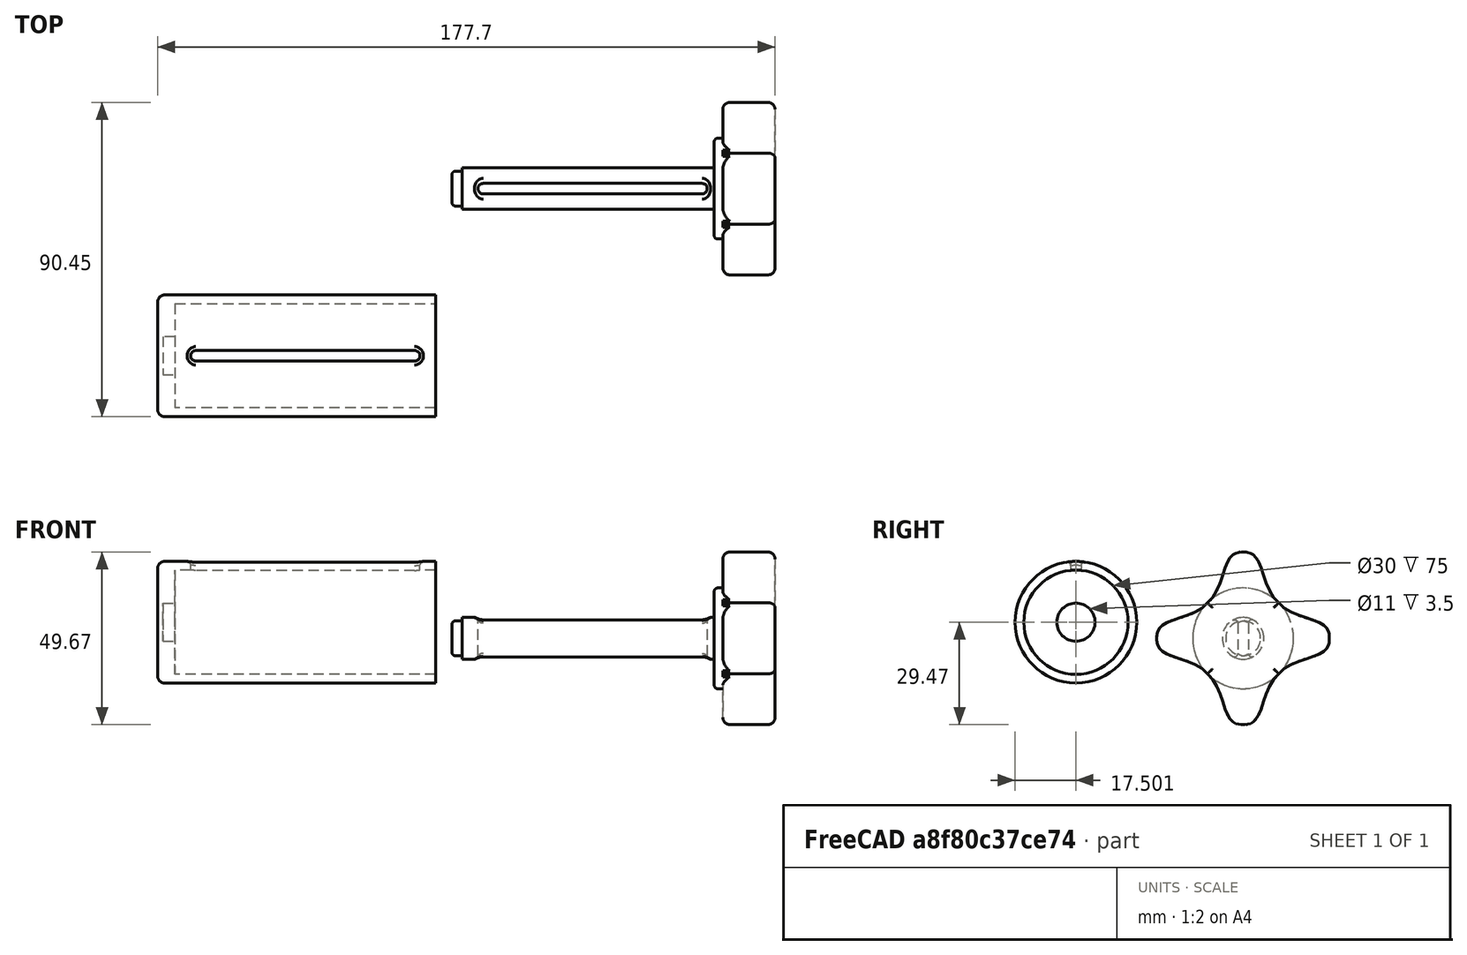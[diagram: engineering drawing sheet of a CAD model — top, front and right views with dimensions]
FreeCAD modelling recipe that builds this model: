
FCSTD DOCUMENT  (FreeCAD 1.0R39285 (Git))
Label: tomato_paste_squeezer
License: All rights reserved
objects: Sketcher::SketchObject×10, PartDesign::Pad×6, PartDesign::Pocket×4, PartDesign::Fillet×4, PartDesign::Body×2, App::Link×2, App::FeaturePython×2, PartDesign::Plane×1, PartDesign::PolarPattern×1, Assembly::JointGroup×1, Assembly::AssemblyObject×1
note: 67 computed .brp shape members not serialized (recipe doc carries the construction recipe); baked Part::Feature solids carry a one-line shape summary decoded from their .brp

FEATURE [Sketcher::SketchObject] Sketch
  ArcFitTolerance = 1e-06
  AttachmentSupport = -> [YZ_Plane]
  FullyConstrained = true
  MakeInternals = false
  MapMode = 5
  Placement = pos=(0,0,0) rot=(0.57735,0.57735,0.57735;2.0944rad)
  sketch-geometry (2):
    g0: Circle CenterX=0 CenterY=0 CenterZ=0 NormalX=0 NormalY=0 NormalZ=1 AngleXU=0 Radius=15
    g1: Circle CenterX=0 CenterY=0 CenterZ=0 NormalX=0 NormalY=0 NormalZ=1 AngleXU=0 Radius=17.5
  constraints (4):
    c: Diameter(g0) = 30
    c: Coincident(g0,g-1)
    c: Diameter(g1) = 35
    c: Coincident(g1,g0)
FEATURE [PartDesign::Pad] Pad
  Direction = (1,0,0)
  Length = 75
  Length2 = 10
  Placement = pos=(0,0,0) rot=(1,1,1;2.0944rad)
  Profile = -> Sketch
  ReferenceAxis = -> Sketch [N_Axis]
  Refine = true
  Suppressed = false
  Type = 0
FEATURE [PartDesign::Plane] DatumPlane
  AttachmentOffset = pos=(0,0,17.5) rot=(0,0,1;0rad)
  AttachmentSupport = -> [XY_Plane]
  Length = 114.142
  MapMode = 5
  Placement = pos=(0,0,17.5) rot=(0,0,1;0rad)
  ResizeMode = 0
  Width = 64.1421
FEATURE [Sketcher::SketchObject] Sketch001
  ArcFitTolerance = 1e-06
  AttachmentSupport = -> [DatumPlane]
  ExternalGeometry = -> [Pad]
  FullyConstrained = true
  MakeInternals = false
  MapMode = 5
  Placement = pos=(0,0,17.5) rot=(0,0,1;0rad)
  sketch-geometry (4):
    g0: ArcOfCircle CenterX=6 CenterY=0 CenterZ=0 NormalX=0 NormalY=0 NormalZ=1 AngleXU=0 Radius=1.5 StartAngle=1.5708 EndAngle=4.71239
    g1: ArcOfCircle CenterX=69 CenterY=0 CenterZ=0 NormalX=0 NormalY=0 NormalZ=1 AngleXU=0 Radius=1.5 StartAngle=4.71239 EndAngle=7.85398
    g2: LineSegment StartX=6 StartY=1.5 StartZ=0 EndX=69 EndY=1.5 EndZ=0
    g3: LineSegment StartX=6 StartY=-1.5 StartZ=0 EndX=69 EndY=-1.5 EndZ=0
  constraints (10):
    c: Tangent(g0,g2) = 1.5708
    c: Tangent(g0,g3) = -1.5708
    c: Tangent(g1,g2) = 1.5708
    c: Tangent(g1,g3) = -1.5708
    c: Equal(g0,g1)
    c: Horizontal(g3)
    c: Radius(g0) = 1.5
    c: PointOnObject(g0,g-1)
    c: DistanceX(g2,g2) = 63
    c: Distance(g0,g-1) = 6
FEATURE [PartDesign::Pocket] Pocket
  BaseFeature = -> Pad
  Direction = (0,0,-1)
  Length = 5
  Length2 = 5
  Placement = pos=(0,0,0) rot=(1,1,1;2.0944rad)
  Profile = -> Sketch001
  ReferenceAxis = -> Sketch001 [N_Axis]
  Refine = true
  Suppressed = false
  Type = 2
FEATURE [Sketcher::SketchObject] Sketch002
  ArcFitTolerance = 1e-06
  AttachmentSupport = -> [Pocket]
  FullyConstrained = true
  MakeInternals = false
  MapMode = 5
  Placement = pos=(0,0,0) rot=(0.57735,0.57735,-0.57735;4.18879rad)
  sketch-geometry (1):
    g0: Circle CenterX=0 CenterY=0 CenterZ=0 NormalX=0 NormalY=0 NormalZ=1 AngleXU=0 Radius=17.5
  constraints (2):
    c: Diameter(g0) = 35
    c: Coincident(g0,g-1)
FEATURE [PartDesign::Pad] Pad001
  BaseFeature = -> Pocket
  Direction = (-1,0,0)
  Length = 5
  Length2 = 10
  Placement = pos=(0,0,0) rot=(1,1,1;2.0944rad)
  Profile = -> Sketch002
  ReferenceAxis = -> Sketch002 [N_Axis]
  Refine = true
  Suppressed = false
  Type = 0
FEATURE [Sketcher::SketchObject] Sketch003
  ArcFitTolerance = 1e-06
  AttachmentSupport = -> [YZ_Plane001]
  FullyConstrained = true
  MakeInternals = false
  MapMode = 5
  Placement = pos=(0,0,0) rot=(0.57735,0.57735,0.57735;2.0944rad)
  sketch-geometry (1):
    g0: Circle CenterX=0 CenterY=0 CenterZ=0 NormalX=0 NormalY=0 NormalZ=1 AngleXU=0 Radius=14.5
  constraints (2):
    c: Diameter(g0) = 29
    c: Coincident(g0,g-1)
FEATURE [PartDesign::Pad] Pad002
  Direction = (1,0,0)
  Length = 2.5
  Length2 = 10
  Placement = pos=(0,0,0) rot=(1,1,1;2.0944rad)
  Profile = -> Sketch003
  ReferenceAxis = -> Sketch003 [N_Axis]
  Refine = true
  Suppressed = false
  Type = 0
FEATURE [Sketcher::SketchObject] Sketch004
  ArcFitTolerance = 1e-06
  AttachmentSupport = -> [Pad002]
  FullyConstrained = true
  MakeInternals = false
  MapMode = 5
  Placement = pos=(2.5,-6e-16,3e-16) rot=(0.57735,0.57735,0.57735;2.0944rad)
  sketch-geometry (1):
    g0: Circle CenterX=0 CenterY=0 CenterZ=0 NormalX=0 NormalY=0 NormalZ=1 AngleXU=0 Radius=25
  constraints (2):
    c: Diameter(g0) = 50
    c: Coincident(g0,g-1)
FEATURE [PartDesign::Pad] Pad003
  BaseFeature = -> Pad002
  Direction = (1,0,0)
  Length = 15
  Length2 = 10
  Placement = pos=(0,0,0) rot=(1,1,1;2.0944rad)
  Profile = -> Sketch004
  ReferenceAxis = -> Sketch004 [N_Axis]
  Refine = true
  Suppressed = false
  Type = 0
FEATURE [Sketcher::SketchObject] Sketch005
  ArcFitTolerance = 1e-06
  AttachmentSupport = -> [Pad003]
  ExternalGeometry = -> [Pad003]
  FullyConstrained = true
  MakeInternals = false
  MapMode = 5
  Placement = pos=(17.5,-3.9e-15,1.9e-15) rot=(0.57735,0.57735,0.57735;2.0944rad)
  sketch-geometry (20):
    g0: LineSegment [constr] StartX=0 StartY=0 StartZ=0 EndX=-10.253 EndY=10.253 EndZ=0
    g1: LineSegment [constr] StartX=0 StartY=0 StartZ=0 EndX=10.253 EndY=10.253 EndZ=0
    g2: LineSegment [constr] StartX=0 StartY=0 StartZ=0 EndX=0 EndY=25 EndZ=0
    g3-g9: Circle [constr] x7 (B-spline internal-alignment scaffolding for g10; pole/knot coordinates omitted)
    g10: BSplineCurve PolesCount=7 KnotsCount=5 Degree=3 IsPeriodic=0
    g11-g15: GeomPoint [constr] x5 (B-spline internal-alignment scaffolding for g10; pole/knot coordinates omitted)
    g16: LineSegment StartX=-10.253 StartY=10.253 StartZ=0 EndX=-25.253 EndY=25.253 EndZ=0
    g17: LineSegment StartX=-25.253 StartY=25.253 StartZ=0 EndX=0 EndY=46.4 EndZ=0
    g18: LineSegment StartX=0 StartY=46.4 StartZ=0 EndX=25.253 EndY=25.253 EndZ=0
    g19: LineSegment StartX=10.253 StartY=10.253 StartZ=0 EndX=25.253 EndY=25.253 EndZ=0
  constraints (35):
    c: Coincident(g0,g-1)
    c: Coincident(g1,g0)
    c: Angle(g-1,g1) = 0.785398
    c: Angle(g0,g-1) = 0.785398
    c: Coincident(g2,g0)
    c: PointOnObject(g2,g-4)
    c: Vertical(g2)
    c: PointOnObject(g0,g-3)
    c: PointOnObject(g1,g-3)
    c: Weight(g3) = 1
    c: Equal(g3, g4-g9) x6
    c: InternalAlignment(g3-g9 -> g10) x7
    c: InternalAlignment(g11-g15 -> g10) x5
    c: Coincident(g3,g0)
    c: PointOnObject(g4,g-3)
    c: PointOnObject(g5,g-4)
    c: Coincident(g6,g2)
    c: PointOnObject(g7,g-4)
    c: PointOnObject(g8,g-3)
    c: Coincident(g9,g1)
    c: DistanceX(g-1,g8) = 7
    c: DistanceX(g4,g-1) = 7
    c: DistanceX(g-1,g7) = 5
    c: DistanceX(g5,g-1) = 5
    c: Coincident(g16,g10)
    c: Coincident(g17,g16)
    c: PointOnObject(g17,g-2)
    c: Coincident(g18,g17)
    c: Coincident(g19,g10)
    c: Coincident(g19,g18)
    c: Angle(g19,g1) = 3.14159
    c: Angle(g0,g16) = 3.14159
    c: DistanceY(g19,g19) = 15
    c: DistanceY(g16,g16) = 15
    c: DistanceY(g-1,g17) = 46.4
FEATURE [PartDesign::Pocket] Pocket001
  BaseFeature = -> Pad003
  Direction = (-1,0,0)
  Length = 0
  Length2 = 5
  Placement = pos=(0,0,0) rot=(1,1,1;2.0944rad)
  Profile = -> Sketch005
  ReferenceAxis = -> Sketch005 [N_Axis]
  Refine = true
  Suppressed = false
  Type = 3
  UpToFace = -> Pad003 [Face3]
FEATURE [PartDesign::PolarPattern] PolarPattern
  Angle = 360
  Axis = -> Sketch005 [N_Axis]
  BaseFeature = -> Pocket001
  Mode = 0
  Occurrences = 4
  Offset = 120
  Originals = -> [Pocket001]
  Placement = pos=(0,0,0) rot=(1,1,1;2.0944rad)
  Refine = true
  Suppressed = false
  TransformMode = 0
FEATURE [Sketcher::SketchObject] Sketch006
  ArcFitTolerance = 1e-06
  AttachmentSupport = -> [PolarPattern]
  FullyConstrained = true
  MakeInternals = false
  MapMode = 5
  Placement = pos=(0,0,0) rot=(0.57735,0.57735,-0.57735;4.18879rad)
  sketch-geometry (1):
    g0: Circle CenterX=0 CenterY=0 CenterZ=0 NormalX=0 NormalY=0 NormalZ=1 AngleXU=0 Radius=6
  constraints (2):
    c: Diameter(g0) = 12
    c: Coincident(g0,g-1)
FEATURE [PartDesign::Pad] Pad004
  BaseFeature = -> PolarPattern
  Direction = (-1,0,0)
  Length = 72.5
  Length2 = 10
  Placement = pos=(0,0,0) rot=(1,1,1;2.0944rad)
  Profile = -> Sketch006 [Edge1]
  ReferenceAxis = -> Sketch006 [N_Axis]
  Refine = true
  Suppressed = false
  Type = 0
FEATURE [Sketcher::SketchObject] Sketch007
  ArcFitTolerance = 1e-06
  AttachmentSupport = -> [XY_Plane001]
  ExternalGeometry = -> [Pad004]
  FullyConstrained = true
  MakeInternals = false
  MapMode = 5
  sketch-geometry (4):
    g0: ArcOfCircle CenterX=-66.5 CenterY=1e-16 CenterZ=0 NormalX=0 NormalY=0 NormalZ=1 AngleXU=0 Radius=1.5 StartAngle=1.5708 EndAngle=4.71239
    g1: ArcOfCircle CenterX=-3.5 CenterY=0 CenterZ=0 NormalX=0 NormalY=0 NormalZ=1 AngleXU=0 Radius=1.5 StartAngle=4.71239 EndAngle=7.85398
    g2: LineSegment StartX=-66.5 StartY=1.5 StartZ=0 EndX=-3.5 EndY=1.5 EndZ=0
    g3: LineSegment StartX=-66.5 StartY=-1.5 StartZ=0 EndX=-3.5 EndY=-1.5 EndZ=0
  constraints (10):
    c: Tangent(g0,g2) = 1.5708
    c: Tangent(g0,g3) = -1.5708
    c: Tangent(g1,g2) = 1.5708
    c: Tangent(g1,g3) = -1.5708
    c: Equal(g0,g1)
    c: Radius(g0) = 1.5
    c: Horizontal(g2)
    c: PointOnObject(g1,g-1)
    c: DistanceX(g2,g2) = 63
    c: Distance(g1,g-3) = 6
FEATURE [PartDesign::Pocket] Pocket002
  BaseFeature = -> Pad004
  Direction = (0,0,-1)
  Length = 5
  Length2 = 5
  Midplane = true
  Placement = pos=(0,0,0) rot=(1,1,1;2.0944rad)
  Profile = -> Sketch007
  ReferenceAxis = -> Sketch007 [N_Axis]
  Refine = true
  Suppressed = false
  Type = 1
FEATURE [Sketcher::SketchObject] Sketch008
  ArcFitTolerance = 1e-06
  AttachmentSupport = -> [Pocket002]
  FullyConstrained = true
  MakeInternals = false
  MapMode = 5
  Placement = pos=(-72.5,3.22e-14,-1.61e-14) rot=(0.57735,0.57735,-0.57735;4.18879rad)
  sketch-geometry (1):
    g0: Circle CenterX=0 CenterY=0 CenterZ=0 NormalX=0 NormalY=0 NormalZ=1 AngleXU=0 Radius=5
  constraints (2):
    c: Diameter(g0) = 10
    c: Coincident(g0,g-1)
FEATURE [PartDesign::Pad] Pad005
  BaseFeature = -> Pocket002
  Direction = (-1,0,0)
  Length = 3
  Length2 = 10
  Placement = pos=(0,0,0) rot=(1,1,1;2.0944rad)
  Profile = -> Sketch008
  ReferenceAxis = -> Sketch008 [N_Axis]
  Refine = true
  Suppressed = false
  Type = 0
FEATURE [Sketcher::SketchObject] Sketch009
  ArcFitTolerance = 1e-06
  AttachmentSupport = -> [Pad001]
  FullyConstrained = true
  MakeInternals = false
  MapMode = 5
  Placement = pos=(0,0,0) rot=(0.57735,0.57735,0.57735;2.0944rad)
  sketch-geometry (1):
    g0: Circle CenterX=0 CenterY=0 CenterZ=0 NormalX=0 NormalY=0 NormalZ=1 AngleXU=0 Radius=5.5
  constraints (2):
    c: Diameter(g0) = 11
    c: Coincident(g0,g-1)
FEATURE [PartDesign::Pocket] Pocket003
  BaseFeature = -> Pad001
  Direction = (-1,0,0)
  Length = 3.5
  Length2 = 5
  Placement = pos=(0,0,0) rot=(1,1,1;2.0944rad)
  Profile = -> Sketch009
  ReferenceAxis = -> Sketch009 [N_Axis]
  Refine = true
  Suppressed = false
  Type = 0
FEATURE [PartDesign::Fillet] Fillet
  Base = -> Pad005 [Edge55,Edge15,Edge43,Edge44]
  BaseFeature = -> Pad005
  Placement = pos=(0,0,0) rot=(1,1,1;2.0944rad)
  Radius = 1
  Refine = true
  SupportTransform = false
  Suppressed = false
  UseAllEdges = false
FEATURE [PartDesign::Fillet] Fillet001
  Base = -> Fillet [Edge25,Edge18,Edge22,Edge34,Edge31,Edge36,Edge28,Edge38]
  BaseFeature = -> Fillet
  Placement = pos=(0,0,0) rot=(1,1,1;2.0944rad)
  Radius = 2
  Refine = true
  SupportTransform = false
  Suppressed = false
  UseAllEdges = false
FEATURE [PartDesign::Body] Body001  label="avvitatore"
  AllowCompound = false
  Group = -> [Sketch003,Pad002,Sketch004,Pad003,Sketch005,Pocket001,PolarPattern,Sketch006,Pad004,Sketch007,Pocket002,Sketch008,Pad005,Fillet,Fillet001]
  Origin = -> Origin001
  Placement = pos=(167.73,280.208,-4.63576) rot=(0,0,1;0rad)
  Tip = -> Fillet001
FEATURE [PartDesign::Fillet] Fillet002
  Base = -> Pocket003 [Edge1]
  BaseFeature = -> Pocket003
  Placement = pos=(0,0,0) rot=(1,1,1;2.0944rad)
  Radius = 2
  Refine = true
  SupportTransform = false
  Suppressed = false
  UseAllEdges = false
FEATURE [App::Link] corpo_principale  label="corpo_principale001"
  LinkedObject = -> Body
FEATURE [App::FeaturePython] GroundedJoint  # Assembly grounded joint (typed FeaturePython)
  ObjectToGround = -> corpo_principale
FEATURE [App::Link] avvitatore  label="avvitatore001"
  LinkPlacement = pos=(72.5,7.3e-15,-1.767e-13) rot=(1,0,0;3.35028rad)
  LinkedObject = -> Body001
  Placement = pos=(72.5,7.3e-15,-1.767e-13) rot=(1,0,0;3.35028rad)
FEATURE [App::FeaturePython] Joint  label="Cylindrical"  # Assembly joint (typed FeaturePython)
  Activated = true
  AngleMax = 0
  AngleMin = 0
  Detach1 = false
  Detach2 = false
  Distance = 0
  Distance2 = 0
  EnableAngleMax = false
  EnableAngleMin = false
  EnableLengthMax = true
  EnableLengthMin = true
  JointType = 2 (Cylindrical)
  LengthMax = 0
  LengthMin = 0
  Placement1 = pos=(2.5,-3.1e-15,-8.5e-15) rot=(-0.707107,0,-0.707107;3.14159rad)
  Reference1 = -> Assembly [avvitatore.Face20,avvitatore.Edge1]
  Reference2 = -> Assembly [corpo_principale.?Face9,corpo_principale.Edge16]
FEATURE [Assembly::JointGroup] Joints
  Group = -> [GroundedJoint,Joint]
FEATURE [Assembly::AssemblyObject] Assembly  label="AssembyTomatoPasteSqueezer"
  Group = -> [Joints,corpo_principale,GroundedJoint,avvitatore,Joint]
  Origin = -> Origin002
  Type = AssembyTomatoPasteSqueezer
FEATURE [PartDesign::Fillet] Fillet003
  Base = -> Fillet002 [Edge9,Edge6]
  BaseFeature = -> Fillet002
  Placement = pos=(0,0,0) rot=(1,1,1;2.0944rad)
  Radius = 1
  Refine = true
  SupportTransform = false
  Suppressed = false
  UseAllEdges = false
FEATURE [PartDesign::Body] Body  label="corpo_principale"
  AllowCompound = false
  Group = -> [Sketch,Pad,DatumPlane,Sketch001,Pocket,Sketch002,Pad001,Sketch009,Pocket003,Fillet002,Fillet003]
  Origin = -> Origin
  Placement = pos=(12.535,232.091,0) rot=(0,0,1;0rad)
  Tip = -> Fillet003
